# Revit family: Door_Entrances-MS-400_NS-250_WS-500-Mid-Rail_Single-Door_Cross-Aluminum
name_source: partatom
category: Doors
units: mm (PartAtom-declared; Revit-internal decimal feet)

## family parameters
Always vertical = Yes
Classification Number = 23.30.10.00
Cut with Voids When Loaded = No
Host = Wall
Room Calculation Point = No
Shared = No

## types (27) — shared parameters
Analytic Construction = <None>
Define Thermal Properties by = Schematic Type
Description = Wide stile monumental doors
Frame Material = Aluminum
Function = Interior
Glass Material = Glass Material
Hori.Frame A Height = 1' - 0"
Hori.Frame B Height = 0' - 0"
Keynote = 08 41 26
Manufacturer = Cross Aluminum
Model = WS-500 ENTRACES
Product Page URL = https://www.arcat.com
Rough Width = 4' - 0"
Side Frame Width = 0' - 0"
Single Glass Thickness = 0' - 0"
Therma Plank Material = Therma Plank
Thickness = 0' - 0"
URL = https://www.crossaluminum.com
W = 0' - 0"
W1 = 4' - 0"
Wall Closure = By host

## per-type parameters (varying)
| type | Double Glass | Frame A | Frame B | H1 | Height | Rough Height | Single Glass | Width |
| WS-500_G-20H/G-20B | Yes | No | Yes | 9' - 0" | 9' - 0" | 9' - 0" | No | 6' - 0" |
| WS-500_G-18H/G-18B | Yes | Yes | No | 9' - 0" | 9' - 0" | 9' - 0" | No | 6' - 0" |
| WS-500_G-16H/G-16B | Yes | Yes | No | 9' - 0" | 9' - 0" | 9' - 0" | No | 6' - 0" |
| WS-500_G-14H/G-14B | Yes | Yes | No | 9' - 0" | 9' - 0" | 9' - 0" | No | 6' - 0" |
| WS-500_G-12H/G-12B | Yes | Yes | No | 9' - 0" | 9' - 0" | 9' - 0" | No | 6' - 0" |
| WS-500_G-10H/G-10B | Yes | No | Yes | 9' - 0" | 9' - 0" | 9' - 0" | No | 6' - 0" |
| WS-500_G-8H/G-8B | Yes | No | Yes | 9' - 0" | 9' - 0" | 9' - 0" | No | 6' - 0" |
| WS-500_G-6H/G-6B | Yes | No | Yes | 9' - 0" | 9' - 0" | 9' - 0" | No | 6' - 0" |
| WS-500_G-6H-MOD/G-6B-MOD | No | No | Yes | 8' - 0" | 8' - 0" | 8' - 0" | Yes | 4' - 0" |
| MS-400_G-6H/G-6B | Yes | No | Yes | 9' - 0" | 9' - 0" | 9' - 0" | No | 6' - 0" |
| MS-400_G-6H-MOD/G-6B-MOD | No | No | Yes | 8' - 0" | 8' - 0" | 8' - 0" | Yes | 4' - 0" |
| MS-400_G-8H/G-8B | Yes | No | Yes | 9' - 0" | 9' - 0" | 9' - 0" | No | 6' - 0" |
| MS-400_G-10H/G-10B | Yes | No | Yes | 9' - 0" | 9' - 0" | 9' - 0" | No | 6' - 0" |
| MS-400_G-12H/G-12B | Yes | Yes | No | 9' - 0" | 9' - 0" | 9' - 0" | No | 6' - 0" |
| MS-400_G-14H/G-14B | Yes | Yes | No | 9' - 0" | 9' - 0" | 9' - 0" | No | 6' - 0" |
| MS-400_G-16H/G-16B | Yes | Yes | No | 9' - 0" | 9' - 0" | 9' - 0" | No | 6' - 0" |
| MS-400_G-18H/G-18B | Yes | Yes | No | 9' - 0" | 9' - 0" | 9' - 0" | No | 6' - 0" |
| MS-400_G-20H/G-20B | Yes | Yes | No | 9' - 0" | 9' - 0" | 9' - 0" | No | 6' - 0" |
| NS-250_G-6H/G-6B | Yes | No | Yes | 9' - 0" | 9' - 0" | 9' - 0" | No | 6' - 0" |
| NS-250_G-6H-MOD/G-6B-MOD | No | No | Yes | 8' - 0" | 8' - 0" | 8' - 0" | Yes | 4' - 0" |
| NS-250_G-8H/G-8B | Yes | No | Yes | 9' - 0" | 9' - 0" | 9' - 0" | No | 6' - 0" |
| NS-250_G-10H/G-10B | Yes | No | Yes | 9' - 0" | 9' - 0" | 9' - 0" | No | 6' - 0" |
| NS-250_G-12H/G-12B | Yes | Yes | No | 9' - 0" | 9' - 0" | 9' - 0" | No | 6' - 0" |
| NS-250_G-14H/G-14B | Yes | Yes | No | 9' - 0" | 9' - 0" | 9' - 0" | No | 6' - 0" |
| NS-250_G-16H/G-16B | Yes | Yes | No | 9' - 0" | 9' - 0" | 9' - 0" | No | 6' - 0" |
| NS-250_G-18H/G-18B | Yes | Yes | No | 9' - 0" | 9' - 0" | 9' - 0" | No | 6' - 0" |
| NS-250_G-20H/G-20B | Yes | Yes | No | 9' - 0" | 9' - 0" | 9' - 0" | No | 6' - 0" |

## geometry (parser evidence)
native form markers: Sweep x22
no freeform markers — native parametric forms only
